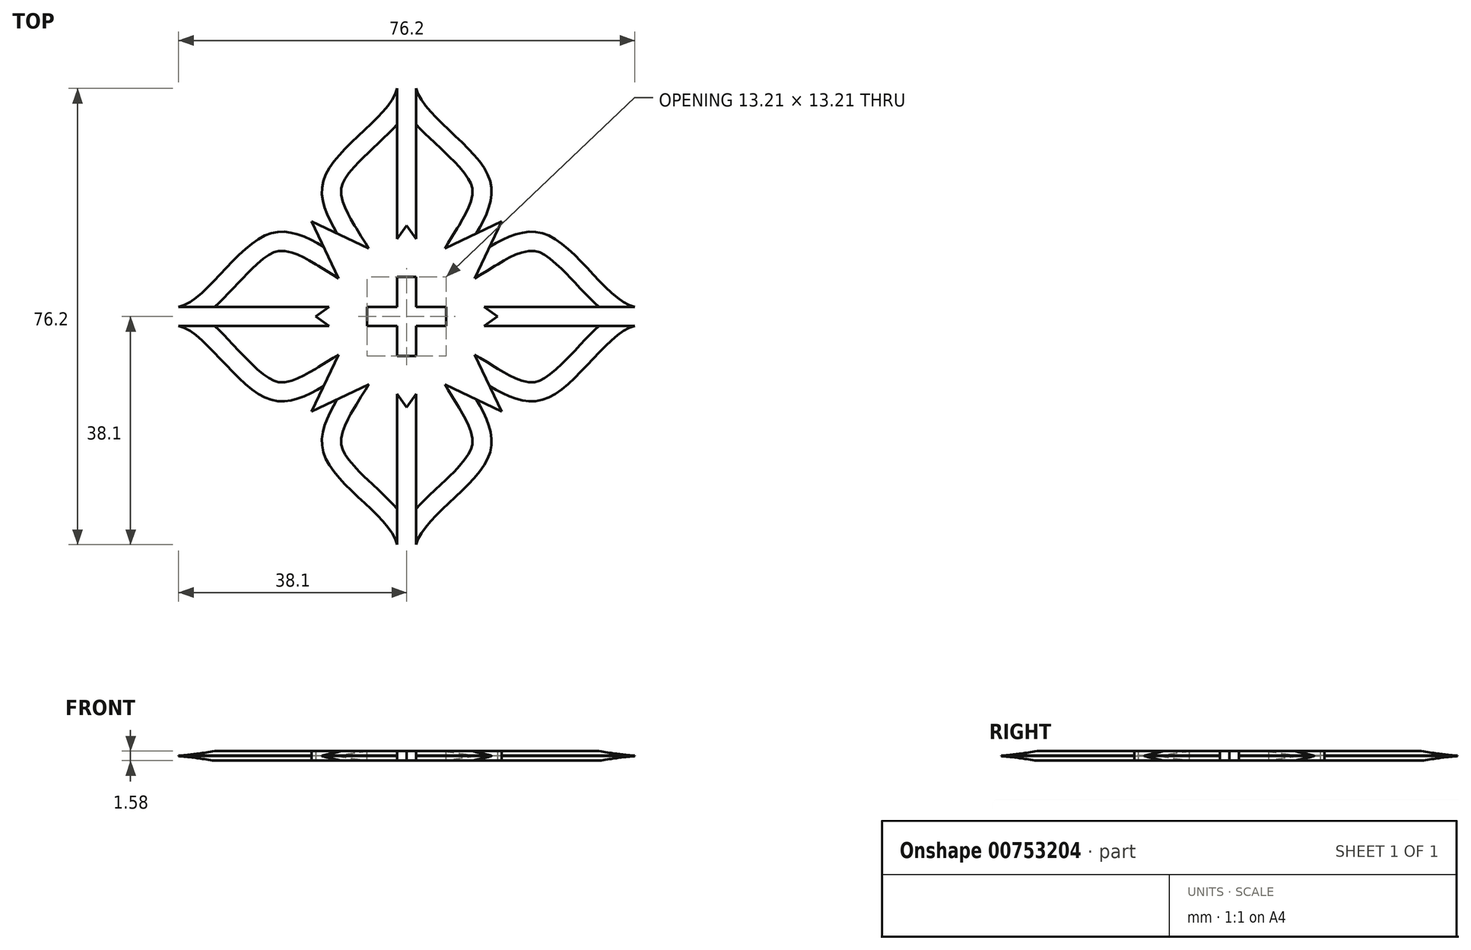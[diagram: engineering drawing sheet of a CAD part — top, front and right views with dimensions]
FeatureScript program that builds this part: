
annotation { "Feature Type Name" : "Feature", "Feature Type Description" : "" }
export const myFeature = defineFeature(function(context is Context, id is Id, definition is map)
    precondition{}
    {
        {
            var Q0;
            Q0=qCreatedBy(makeId("Top.planeOp"),FACE);
            var sketch = newSketch(context, id + "F0", { "sketchPlane" : qUnion([Q0])});
            skCircle(sketch, "E0", {"center": v(0, 0) * mm, "radius": 50.8 * mm, "construction": true});
            skLineSegment(sketch, "E1", {"start": v(0, 0) * mm, "end": v(1.59, 0) * mm, "construction": true});
            skLineSegment(sketch, "E2", {"start": v(0, 0) * mm, "end": v(0, 3.18) * mm, "construction": true});
            skLineSegment(sketch, "E3", {"start": v(1.59, 38.1) * mm, "end": v(1.59, -38.1) * mm});
            skFitSpline(sketch, "E4", {"points": [v(1.59, 38.1) * mm, v(13.87, 22.82) * mm, v(8.71, 9) * mm, v(6.61, 0) * mm], "startDerivative": vector(7.93, -35.79) * mm, "endDerivative": vector(0, -29.8) * mm});
            skFitSpline(sketch, "E5.MirrorCS", {"points": [v(1.59, -38.1) * mm, v(13.87, -22.82) * mm, v(8.71, -9) * mm, v(6.61, 0) * mm], "startDerivative": vector(7.93, 35.79) * mm, "endDerivative": vector(0, 29.8) * mm});
            skSolve(sketch);
        }
        {
            var Q0;
            Q0=makeQuery(id+"F0.imprint","IMPRINT",FACE,{"disambiguationData":[TD([[makeQuery(id+"F0.imprint","IMPRINT",EDGE,{"derivedFrom":sQuery(id+"F0.wireOp",EDGE,"E3")}),1.0]])]});
            extrude(context, id + "F1", {"entities" : qUnion([Q0]), "endBound" : BoundingType.SYMMETRIC, "depth" : 1.59 * mm, "offsetDistance" : 25.4 * mm});
        }
        {
            var Q0;
            Q0=makeQuery(id+"F1.opExtrude","CAP_EDGE",EDGE,{"disambiguationData":[OSD([sQuery(id+"F0.wireOp",EDGE,"E5.MirrorCS")])],"isStart":false});
            var Q1;
            Q1=makeQuery(id+"F1.opExtrude","CAP_EDGE",EDGE,{"disambiguationData":[OSD([sQuery(id+"F0.wireOp",EDGE,"E5.MirrorCS")])],"isStart":true});
            var Q2;
            Q2=makeQuery(id+"F1.opExtrude","CAP_EDGE",EDGE,{"disambiguationData":[OSD([sQuery(id+"F0.wireOp",EDGE,"E4")])],"isStart":true});
            var Q3;
            Q3=makeQuery(id+"F1.opExtrude","CAP_EDGE",EDGE,{"disambiguationData":[OSD([sQuery(id+"F0.wireOp",EDGE,"E4")])],"isStart":false});
            chamfer(context, id + "F2", {"entities" : qUnion([Q0, Q1, Q2, Q3]), "chamferType" : ChamferType.TWO_OFFSETS, "width1" : 3.17 * mm, "oppositeDirection" : false, "width2" : 0.76 * mm, "tangentPropagation" : true});
        }
        {
            var Q0;
            Q0=makeQuery(id+"F1.*.split.splitOp","SPLIT",BODY,{"derivedFrom":makeQuery(id+"F1.opExtrude","SWEPT_BODY",BODY,{"disambiguationData":[OSD([sQuery(id+"F0.wireOp",EDGE,"E3"),sQuery(id+"F0.wireOp",EDGE,"E4"),sQuery(id+"F0.wireOp",EDGE,"E5.MirrorCS")])]})});
            var Q1;
            Q1=qCreatedBy(makeId("Right.planeOp"),FACE);
            mirror(context, id + "F3", {"entities" : qUnion([Q0]), "mirrorPlane" : qUnion([Q1])});
        }
        {
            var Q0;
            Q0=qCreatedBy(makeId("Front.planeOp"),FACE);
            var sketch = newSketch(context, id + "F4", { "sketchPlane" : qUnion([Q0])});
            skLineSegment(sketch, "E6", {"start": v(0, 0) * mm, "end": v(0, 11.1) * mm, "construction": true});
            skSolve(sketch);
        }
        {
            var Q0;
            Q0=makeQuery(id+"F1.*.split.splitOp","SPLIT",BODY,{"derivedFrom":makeQuery(id+"F1.opExtrude","SWEPT_BODY",BODY,{"disambiguationData":[OSD([sQuery(id+"F0.wireOp",EDGE,"E3"),sQuery(id+"F0.wireOp",EDGE,"E4"),sQuery(id+"F0.wireOp",EDGE,"E5.MirrorCS")])]})});
            var Q1;
            Q1=makeQuery(id+"F3.opPattern","COPY",BODY,{"derivedFrom":makeQuery(id+"F1.*.split.splitOp","SPLIT",BODY,{"derivedFrom":makeQuery(id+"F1.opExtrude","SWEPT_BODY",BODY,{"disambiguationData":[OSD([sQuery(id+"F0.wireOp",EDGE,"E3"),sQuery(id+"F0.wireOp",EDGE,"E4"),sQuery(id+"F0.wireOp",EDGE,"E5.MirrorCS")])]})}),"instanceName":"1"});
            var Q2;
            Q2=sQuery(id+"F4.wireOp",EDGE,"E6");
            circularPattern(context, id + "F5", {"entities" : qUnion([Q0, Q1]), "axis" : qUnion([Q2]), "angle" : 90 * degree, "instanceCount" : 2, "equalSpace" : true});
        }
        {
            var Q0;
            Q0=qCreatedBy(makeId("Top.planeOp"),FACE);
            var sketch = newSketch(context, id + "F6", { "sketchPlane" : qUnion([Q0])});
            skLineSegment(sketch, "E7.bottom", {"start": v(15.88, -15.88) * mm, "end": v(-15.87, -15.88) * mm, "construction": true});
            skLineSegment(sketch, "E7.top", {"start": v(15.87, 15.88) * mm, "end": v(-15.88, 15.87) * mm, "construction": true});
            skLineSegment(sketch, "E7.left", {"start": v(15.88, -15.88) * mm, "end": v(15.87, 15.88) * mm, "construction": true});
            skLineSegment(sketch, "E7.right", {"start": v(-15.87, -15.88) * mm, "end": v(-15.88, 15.88) * mm, "construction": true});
            skPoint(sketch, "E7.middle", {"position": v(0, 0) * mm});
            skLineSegment(sketch, "E8", {"start": v(-15.88, 15.88) * mm, "end": v(-3.65, 10.06) * mm});
            skLineSegment(sketch, "E9", {"start": v(-3.65, 10.06) * mm, "end": v(0, 15.18) * mm});
            skLineSegment(sketch, "E10", {"start": v(-15.88, 15.88) * mm, "end": v(15.88, -15.88) * mm, "construction": true});
            skLineSegment(sketch, "E11.MirrorCS", {"start": v(-15.87, 15.88) * mm, "end": v(-10.06, 3.65) * mm});
            skLineSegment(sketch, "E12.MirrorCS", {"start": v(-10.06, 3.65) * mm, "end": v(-15.18, 0) * mm});
            skLineSegment(sketch, "E13.MirrorCS", {"start": v(3.65, 10.06) * mm, "end": v(0, 15.18) * mm});
            skLineSegment(sketch, "E14.MirrorCS", {"start": v(15.88, 15.88) * mm, "end": v(3.65, 10.06) * mm});
            skLineSegment(sketch, "E15.MirrorCS", {"start": v(15.88, 15.88) * mm, "end": v(10.06, 3.65) * mm});
            skLineSegment(sketch, "E16.MirrorCS", {"start": v(10.06, 3.65) * mm, "end": v(15.18, 0) * mm});
            skLineSegment(sketch, "E17.MirrorCS", {"start": v(-10.06, -3.65) * mm, "end": v(-15.18, 0) * mm});
            skLineSegment(sketch, "E18.MirrorCS", {"start": v(-15.88, -15.88) * mm, "end": v(-10.06, -3.65) * mm});
            skLineSegment(sketch, "E19.MirrorCS", {"start": v(-15.88, -15.88) * mm, "end": v(-3.65, -10.06) * mm});
            skLineSegment(sketch, "E20.MirrorCS", {"start": v(-3.65, -10.06) * mm, "end": v(0, -15.18) * mm});
            skLineSegment(sketch, "E21.MirrorCS", {"start": v(3.65, -10.06) * mm, "end": v(0, -15.18) * mm});
            skLineSegment(sketch, "E22.MirrorCS", {"start": v(15.88, -15.88) * mm, "end": v(3.65, -10.06) * mm});
            skLineSegment(sketch, "E23.MirrorCS", {"start": v(15.88, -15.88) * mm, "end": v(10.06, -3.65) * mm});
            skLineSegment(sketch, "E24.MirrorCS", {"start": v(10.06, -3.65) * mm, "end": v(15.18, 0) * mm});
            skSolve(sketch);
        }
        {
            var Q0;
            Q0=makeQuery(id+"F6.imprint","IMPRINT",FACE,{"disambiguationData":[TD([[makeQuery(id+"F6.imprint","IMPRINT",EDGE,{"derivedFrom":sQuery(id+"F6.wireOp",EDGE,"E8")}),-1.0]])]});
            extrude(context, id + "F7", {"entities" : qUnion([Q0]), "endBound" : BoundingType.SYMMETRIC, "depth" : 1.59 * mm, "offsetDistance" : 25.4 * mm});
        }
        {
            var Q0;
            Q0=makeQuery(id+"F1.opExtrude","SWEPT_BODY",BODY,{"disambiguationData":[OSD([sQuery(id+"F0.wireOp",EDGE,"E3"),sQuery(id+"F0.wireOp",EDGE,"E4"),sQuery(id+"F0.wireOp",EDGE,"E5.MirrorCS")])]});
            var Q1;
            Q1=makeQuery(id+"F3.opPattern","COPY",BODY,{"derivedFrom":makeQuery(id+"F1.opExtrude","SWEPT_BODY",BODY,{"disambiguationData":[OSD([sQuery(id+"F0.wireOp",EDGE,"E3"),sQuery(id+"F0.wireOp",EDGE,"E4"),sQuery(id+"F0.wireOp",EDGE,"E5.MirrorCS")])]}),"instanceName":"1"});
            var Q2;
            Q2=makeQuery(id+"F5.opPattern","COPY",BODY,{"derivedFrom":makeQuery(id+"F1.opExtrude","SWEPT_BODY",BODY,{"disambiguationData":[OSD([sQuery(id+"F0.wireOp",EDGE,"E3"),sQuery(id+"F0.wireOp",EDGE,"E4"),sQuery(id+"F0.wireOp",EDGE,"E5.MirrorCS")])]}),"instanceName":"1"});
            var Q3;
            Q3=makeQuery(id+"F5.opPattern","COPY",BODY,{"derivedFrom":makeQuery(id+"F3.opPattern","COPY",BODY,{"derivedFrom":makeQuery(id+"F1.opExtrude","SWEPT_BODY",BODY,{"disambiguationData":[OSD([sQuery(id+"F0.wireOp",EDGE,"E3"),sQuery(id+"F0.wireOp",EDGE,"E4"),sQuery(id+"F0.wireOp",EDGE,"E5.MirrorCS")])]}),"instanceName":"1"}),"instanceName":"1"});
            var Q4;
            Q4=makeQuery(id+"F7.*.split.splitOp","SPLIT",BODY,{"derivedFrom":makeQuery(id+"F7.opExtrude","SWEPT_BODY",BODY,{"disambiguationData":[OSD([sQuery(id+"F6.wireOp",EDGE,"E8"),sQuery(id+"F6.wireOp",EDGE,"E9"),sQuery(id+"F6.wireOp",EDGE,"E11.MirrorCS"),sQuery(id+"F6.wireOp",EDGE,"E12.MirrorCS"),sQuery(id+"F6.wireOp",EDGE,"E13.MirrorCS"),sQuery(id+"F6.wireOp",EDGE,"E14.MirrorCS"),sQuery(id+"F6.wireOp",EDGE,"E15.MirrorCS"),sQuery(id+"F6.wireOp",EDGE,"E16.MirrorCS"),sQuery(id+"F6.wireOp",EDGE,"E17.MirrorCS"),sQuery(id+"F6.wireOp",EDGE,"E18.MirrorCS"),sQuery(id+"F6.wireOp",EDGE,"E19.MirrorCS"),sQuery(id+"F6.wireOp",EDGE,"E20.MirrorCS"),sQuery(id+"F6.wireOp",EDGE,"E21.MirrorCS"),sQuery(id+"F6.wireOp",EDGE,"E22.MirrorCS"),sQuery(id+"F6.wireOp",EDGE,"E23.MirrorCS"),sQuery(id+"F6.wireOp",EDGE,"E24.MirrorCS")])]})});
            booleanBodies(context, id + "F8", {"operationType" : BooleanOperationType.UNION, "tools" : qUnion([Q0, Q1, Q2, Q3, Q4])});
        }
        {
            var Q0;
            {var subQ0=makeQuery(id+"F1.opExtrude","CAP_FACE",FACE,{"disambiguationData":[OSD([sQuery(id+"F0.wireOp",EDGE,"E3"),sQuery(id+"F0.wireOp",EDGE,"E4"),sQuery(id+"F0.wireOp",EDGE,"E5.MirrorCS")])],"isStart":false});var subQ1=makeQuery(id+"F3.opPattern","COPY",FACE,{"derivedFrom":subQ0,"instanceName":"1"});Q0=makeQuery(id+"F8.opBoolean","MERGE",FACE,{"derivedFrom":[subQ0,subQ1,makeQuery(id+"F5.opPattern","COPY",FACE,{"derivedFrom":subQ0,"instanceName":"1"}),makeQuery(id+"F5.opPattern","COPY",FACE,{"derivedFrom":subQ1,"instanceName":"1"}),makeQuery(id+"F7.opExtrude","CAP_FACE",FACE,{"disambiguationData":[OSD([sQuery(id+"F6.wireOp",EDGE,"E8"),sQuery(id+"F6.wireOp",EDGE,"E9"),sQuery(id+"F6.wireOp",EDGE,"E11.MirrorCS"),sQuery(id+"F6.wireOp",EDGE,"E12.MirrorCS"),sQuery(id+"F6.wireOp",EDGE,"E13.MirrorCS"),sQuery(id+"F6.wireOp",EDGE,"E14.MirrorCS"),sQuery(id+"F6.wireOp",EDGE,"E15.MirrorCS"),sQuery(id+"F6.wireOp",EDGE,"E16.MirrorCS"),sQuery(id+"F6.wireOp",EDGE,"E17.MirrorCS"),sQuery(id+"F6.wireOp",EDGE,"E18.MirrorCS"),sQuery(id+"F6.wireOp",EDGE,"E19.MirrorCS"),sQuery(id+"F6.wireOp",EDGE,"E20.MirrorCS"),sQuery(id+"F6.wireOp",EDGE,"E21.MirrorCS"),sQuery(id+"F6.wireOp",EDGE,"E22.MirrorCS"),sQuery(id+"F6.wireOp",EDGE,"E23.MirrorCS"),sQuery(id+"F6.wireOp",EDGE,"E24.MirrorCS")])],"isStart":false})]});}
            var sketch = newSketch(context, id + "F9", { "sketchPlane" : qUnion([Q0])});
            skLineSegment(sketch, "E25.bottom", {"start": v(1.59, -6.6) * mm, "end": v(-1.59, -6.6) * mm});
            skLineSegment(sketch, "E25.top", {"start": v(1.59, 6.6) * mm, "end": v(-1.59, 6.6) * mm});
            skLineSegment(sketch, "E25.left", {"start": v(1.59, -6.6) * mm, "end": v(1.59, -1.59) * mm});
            skLineSegment(sketch, "E25.right", {"start": v(-1.59, -6.6) * mm, "end": v(-1.59, -1.59) * mm});
            skPoint(sketch, "E25.middle", {"position": v(0, 0) * mm});
            skLineSegment(sketch, "E26.bottom", {"start": v(6.6, -1.59) * mm, "end": v(1.59, -1.59) * mm});
            skLineSegment(sketch, "E26.top", {"start": v(6.6, 1.59) * mm, "end": v(1.59, 1.59) * mm});
            skLineSegment(sketch, "E26.left", {"start": v(6.6, -1.59) * mm, "end": v(6.6, 1.59) * mm});
            skLineSegment(sketch, "E26.right", {"start": v(-6.6, -1.59) * mm, "end": v(-6.6, 1.59) * mm});
            skLineSegment(sketch, "E27.trimOffspring", {"start": v(-1.59, 1.59) * mm, "end": v(-6.6, 1.59) * mm});
            skLineSegment(sketch, "E28.trimOffspring", {"start": v(-1.59, 1.59) * mm, "end": v(-1.59, 6.6) * mm});
            skLineSegment(sketch, "E29.trimOffspring", {"start": v(-1.59, -1.59) * mm, "end": v(-6.6, -1.59) * mm});
            skLineSegment(sketch, "E30.trimOffspring", {"start": v(1.59, 1.59) * mm, "end": v(1.59, 6.6) * mm});
            skLineSegment(sketch, "E31", {"start": v(-1.59, 6.6) * mm, "end": v(-6.6, 1.59) * mm, "construction": true});
            skLineSegment(sketch, "E32", {"start": v(-11.13, 13.62) * mm, "end": v(-13.62, 11.13) * mm, "construction": true});
            skLineSegment(sketch, "E33", {"start": v(-12.38, 12.38) * mm, "end": v(-4.1, 4.1) * mm, "construction": true});
            skSolve(sketch);
        }
        {
            var Q0;
            Q0=makeQuery(id+"F9.imprint","IMPRINT",FACE,{"disambiguationData":[TD([[makeQuery(id+"F9.imprint","IMPRINT",EDGE,{"derivedFrom":sQuery(id+"F9.wireOp",EDGE,"E25.bottom")}),-1.0]])]});
            extrude(context, id + "F10", {"entities" : qUnion([Q0]), "operationType" : NewBodyOperationType.REMOVE, "oppositeDirection" : true, "depth" : 25.4 * mm, "offsetDistance" : 25.4 * mm});
        }
    });
